# Revit family: QF_EGRO_TOP_MILK_FRIDGE
name_source: partatom
category: Specialty Equipment
revit_build: Autodesk Revit 2015 (Build: 20140606_1530(x64)
units: mm (PartAtom-declared; Revit-internal decimal feet)

## types (1)
- QF_EGRO_TOP_MILK_FRIDGE
    Apparent Power = 0 VA
    Cold Water Connection Height = 0 "
    Cold Water Flow = 0 GPM
    Cold Water Maximum Pressure = 0.00 psi
    Cold Water Minimum Pressure = 0.00 psi
    Cold Water RI Height = 0 "
    Cold Water Size = 0"
    Cold Water Temperature Recommended = -460 °F
    Conn Conduit = Yes
    Conn Plug = Typ 25 / CEE
    Cycle = 50 Hz
    Depth = 20.27 "
    Description = TOP MILK FRIDGE
    Elec Conn Connection Height = 0 "
    Elec Conn RI Height = 0 "
    FL Amps = 13 A
    Foodservice Equipment Identifier = Yes
    Height = 31 "
    Identify Quantity as Lot = Yes
    Indirect Waste Connection Height = 0 "
    Indirect Waste Flow = 0 GPM
    Indirect Waste Size = 2"
    Length = 11.75 "
    Manufacturer = EGRO
    Max Overcurrent Protection = 0 A
    Min Ckt Ampacity = 0 A
    Model = TOP MILK FRIDGE
    Number of Poles = 1
    Phase = 1
    Volts = 220 V
    Watts = 3200 W
    Weight in Kilograms = 29

## geometry (parser evidence)
native form markers: Blend x12, Sweep x6
no freeform markers — native parametric forms only
